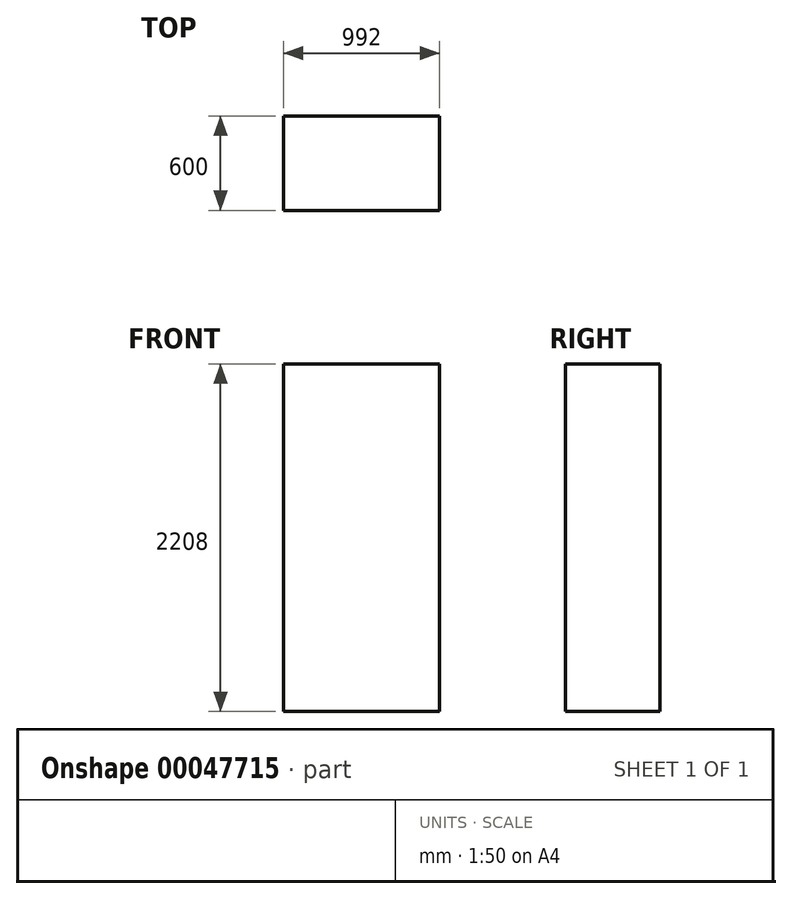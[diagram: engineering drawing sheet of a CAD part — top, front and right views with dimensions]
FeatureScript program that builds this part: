
annotation { "Feature Type Name" : "Feature", "Feature Type Description" : "" }
export const myFeature = defineFeature(function(context is Context, id is Id, definition is map)
    precondition{}
    {
        {
            var Q0;
            Q0=qCreatedBy(makeId("Front.planeOp"),FACE);
            var sketch = newSketch(context, id + "F0", { "sketchPlane" : qUnion([Q0])});
            skLineSegment(sketch, "E0.bottom", {"start": v(0, 0) * mm, "end": v(992, 0) * mm});
            skLineSegment(sketch, "E0.top", {"start": v(0, -2208) * mm, "end": v(992, -2208) * mm});
            skLineSegment(sketch, "E0.left", {"start": v(0, 0) * mm, "end": v(0, -2208) * mm});
            skLineSegment(sketch, "E0.right", {"start": v(992, 0) * mm, "end": v(992, -2208) * mm});
            skSolve(sketch);
        }
        {
            var Q0;
            Q0 = qSketchRegion(id + "F0", true);
            extrude(context, id + "F1", {"entities" : qUnion([Q0]), "depth" : 600 * mm});
        }
    });
